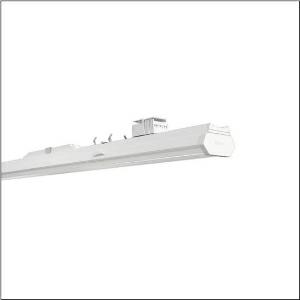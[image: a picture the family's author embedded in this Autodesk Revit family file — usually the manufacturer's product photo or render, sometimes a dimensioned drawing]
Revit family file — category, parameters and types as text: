
# Revit family: licross_r__11_protected_ho_51tp12dn4exl3c_b05a
name_source: partatom
category: Lighting Fixtures
units: mm (PartAtom-declared; Revit-internal decimal feet)

## family parameters
Cut with Voids When Loaded = No
Host = Face
Light Source = No
Part Type = Normal
Room Calculation Point = No
Round Connector Dimension = Use Diameter
Shared = No

## types (1)
- --- (1 x LED, 850 lm, 5 W, 4000K)
    Apparent Load = 5 VA
    CIE Flux Codes = 70 91 97 98 100
    Color Rendering = 80
    Color Temperature = 4000K
    Default Elevation = 1800 mm
    Description = Licross® 11 Protected HO, luminaire insert, of sheet steel, galvanised, coil coated, white, length: 1.500mm, width: 90mm, height: 101mm, LED rated luminous flux: 14.070lm, light colour: 840, control gear: DALI 2, control gear: ECG DALI, with plug, 6-pole, with phase selection, for trunking rail, 14-core, mains connection: 220..240V, AC/DC, 0/50..60Hz, halogen-free wiring, for emergency light function, charging phase on R (wire number 6), converter,control gear: single battery element, battery: LiFeP04, 9Ah, primary optical cover: cover, of PMMA, light emission: direct with ceiling illumination distribution, protection rating (complete): IP64, insulation class (complete): insulation class I (protective earthing), certification: CE, UKCA, protection symbol: D if used in an environment with conductive dust loads with corresponding accessories, permissible ambient temperature for indoor applications: +5..+30°C, standard: EN 60598-2-22, corresponds to IFS (International Featured Standards) requirements for safety and quality in the food industry, reducing of maximum allowable ambient temperature of 5°C with ceiling mounting, LABS conformity tested according to VDMA 24364:2018-05, packaging unit: 1 piece
    Height = 92 mm
    Lamp = 1 x LED
    Lamp Light Flux = 850 lm
    Lamp Power = 5 W
    Lamp count = 1
    Length = 1500 mm
    Luminous efficacy = 170 lm/W
    Manufacturer = Siteco
    ModVariant = No
    Model = 51TP12DN4EXL3C
    Mounting Place = Ceiling
    Mounting Type = Pendant
    Number of Poles = 1
    OnlyDefault = Yes
    Power Factor = 1
    Product Name = Licross® 11 Protected HO
    Product group = luminaire insert
    ProductGroupID = 902
    Protection Class = Protection class I
    Protection Degree = IP 64
    RLX_Detail_Level = 1
    RlxData = <blob elided: 24833 chars, md5=5582479c>
    Socket = socket
    Standby Power = 0 W
    System Light Flux = 850 lm
    System Power = 5 W
    Type Comments = : emergency light operation: 3 h
    Type Image = l_1256148.jpg
    URL = http://relux.com
    VarID = @adj_126125
    Voltage = 0 V
    Weight = 0.00 kg
    Width = 88 mm

## geometry (parser evidence)
native form markers: Blend x4, Sweep x10
no freeform markers — native parametric forms only
